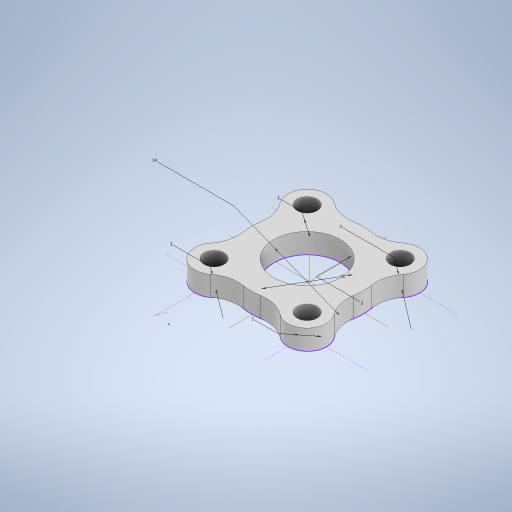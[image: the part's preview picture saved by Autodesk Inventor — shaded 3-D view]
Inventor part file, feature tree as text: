
AUTODESK INVENTOR PART (.ipt)
format: ipt  version: 2024.2 (Build 282272000, 272)  size: 304,128 bytes
history: native  units: mm
features: other x9, extrude x2, sketch x1
ambient origin geometry x8: Origin, YZ Plane, XZ Plane, XY Plane, X Axis, Y Axis, Z Axis, Center Point
bodies: Body1 (feature_tree)
feature tree (12):
  other  "Твердое тело1"
  sketch  "Эскиз1"
  extrude  "Выдавливание1"  Depth=3.0mm TaperAngle=0.0deg
  extrude  "Выдавливание3"  Depth=2.0mm
  other  "Сопряжение грани1"
  other  "Сопряжение грани2"
  other  "Сопряжение грани3"
  other  "Сопряжение грани4"
  other  "Сопряжение грани5"
  other  "Сопряжение грани6"
  other  "Сопряжение грани7"
  other  "Сопряжение грани8"
